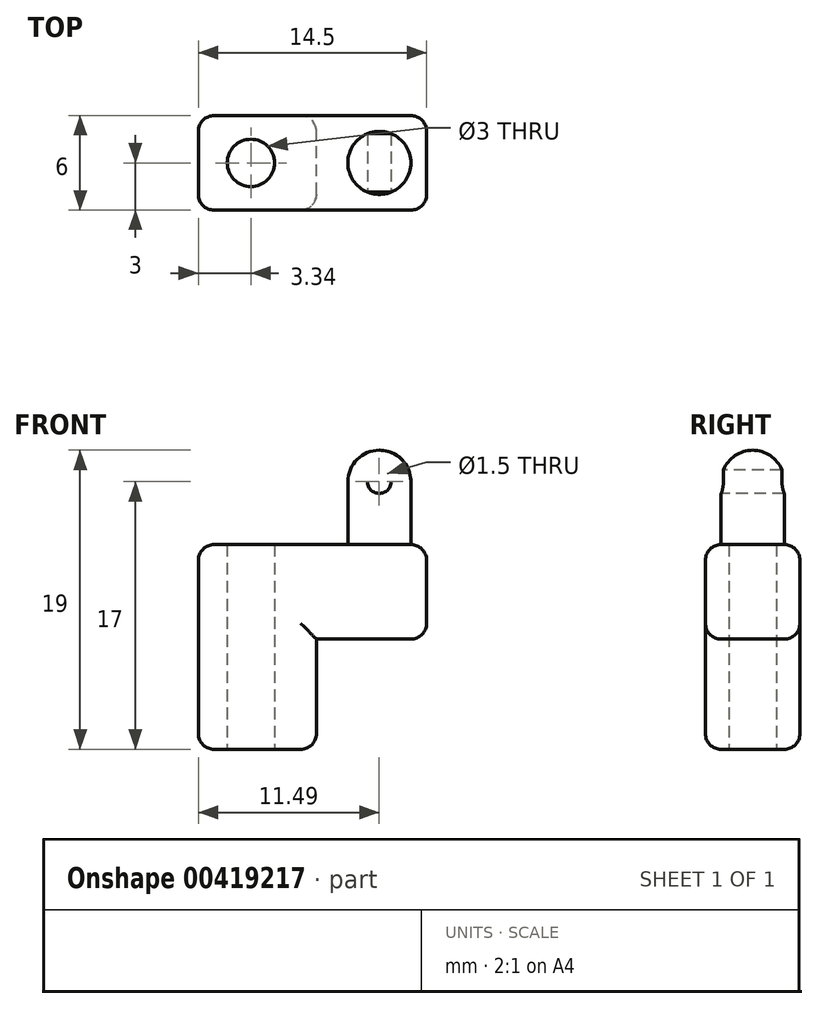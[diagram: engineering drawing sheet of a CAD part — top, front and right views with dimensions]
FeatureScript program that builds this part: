
annotation { "Feature Type Name" : "Feature", "Feature Type Description" : "" }
export const myFeature = defineFeature(function(context is Context, id is Id, definition is map)
    precondition{}
    {
        {
            var Q0;
            Q0=qCreatedBy(makeId("Front.planeOp"),FACE);
            var sketch = newSketch(context, id + "F0", { "sketchPlane" : qUnion([Q0])});
            skLineSegment(sketch, "E0", {"start": v(0, 0) * mm, "end": v(0, 13) * mm});
            skLineSegment(sketch, "E1", {"start": v(0, 13) * mm, "end": v(14.5, 13) * mm});
            skLineSegment(sketch, "E2", {"start": v(14.5, 13) * mm, "end": v(14.5, 7) * mm});
            skLineSegment(sketch, "E3", {"start": v(14.5, 7) * mm, "end": v(7.5, 7) * mm});
            skLineSegment(sketch, "E4", {"start": v(7.5, 7) * mm, "end": v(7.5, 0) * mm});
            skLineSegment(sketch, "E5", {"start": v(7.5, 0) * mm, "end": v(0, 0) * mm});
            skSolve(sketch);
        }
        {
            var Q0;
            Q0 = qSketchRegion(id + "F0", true);
            extrude(context, id + "F1", {"entities" : qUnion([Q0]), "endBound" : BoundingType.SYMMETRIC, "depth" : 6 * mm});
        }
        {
            var Q0;
            Q0=makeQuery(id+"F1.opExtrude","SWEPT_FACE",FACE,{"disambiguationData":[OSD([sQuery(id+"F0.wireOp",EDGE,"E1")])]});
            var sketch = newSketch(context, id + "F2", { "sketchPlane" : qUnion([Q0])});
            skCircle(sketch, "E6", {"center": v(11.5, 0) * mm, "radius": 2 * mm});
            skCircle(sketch, "E7", {"center": v(11.5, 0) * mm, "radius": 3 * mm, "construction": true});
            skSolve(sketch);
        }
        {
            var Q0;
            Q0=makeQuery(id+"F2.imprint","IMPRINT",FACE,{"disambiguationData":[TD([[makeQuery(id+"F2.imprint","IMPRINT",EDGE,{"derivedFrom":sQuery(id+"F2.wireOp",EDGE,"E6")}),1.0]])]});
            extrude(context, id + "F3", {"entities" : qUnion([Q0]), "operationType" : NewBodyOperationType.ADD, "depth" : 6 * mm});
        }
        {
            var Q0;
            Q0=makeQuery(id+"F3.opExtrude","CAP_EDGE",EDGE,{"disambiguationData":[OSD([sQuery(id+"F2.wireOp",EDGE,"E6")])],"isStart":false});
            fillet(context, id + "F4", {"entities" : qUnion([Q0]), "radius" : 2 * mm, "tangentPropagation" : true, "allowEdgeOverflow" : false});
        }
        {
            var Q0;
            Q0=qCreatedBy(makeId("Front.planeOp"),FACE);
            var sketch = newSketch(context, id + "F5", { "sketchPlane" : qUnion([Q0])});
            skCircle(sketch, "E8", {"center": v(11.5, 17) * mm, "radius": 0.75 * mm});
            skLineSegment(sketch, "E9.0", {"start": v(13.5, 17) * mm, "end": v(9.5, 17) * mm});
            skSolve(sketch);
        }
        {
            var Q0;
            Q0 = qSketchRegion(id + "F5", true);
            extrude(context, id + "F6", {"entities" : qUnion([Q0]), "operationType" : NewBodyOperationType.REMOVE, "endBound" : BoundingType.SYMMETRIC, "oppositeDirection" : true, "depth" : 25 * mm});
        }
        {
            var Q0;
            Q0=makeQuery(id+"F1.opExtrude","SWEPT_FACE",FACE,{"disambiguationData":[OSD([sQuery(id+"F0.wireOp",EDGE,"E5")])]});
            var sketch = newSketch(context, id + "F7", { "sketchPlane" : qUnion([Q0])});
            skPoint(sketch, "E10", {"position": v(3.34, 0) * mm});
            skPoint(sketch, "E11", {"position": v(3.34, 3) * mm});
            skSolve(sketch);
        }
        {
            var Q0;
            Q0=sQuery(id+"F7.wireOp",VERTEX,"E10");
            var Q1;
            Q1=makeQuery(id+"F1.opExtrude","SWEPT_BODY",BODY,{"disambiguationData":[OSD([sQuery(id+"F0.wireOp",EDGE,"E0"),sQuery(id+"F0.wireOp",EDGE,"E1"),sQuery(id+"F0.wireOp",EDGE,"E2"),sQuery(id+"F0.wireOp",EDGE,"E3"),sQuery(id+"F0.wireOp",EDGE,"E4"),sQuery(id+"F0.wireOp",EDGE,"E5")])]});
            hole(context, id + "F8", {"style" : HoleStyle.SIMPLE, "endStyle" : HoleEndStyle.THROUGH, "holeDiameter" : 3 * mm, "isTappedThrough" : true, "tappedDepth" : 12 * mm, "tapClearance" : 3, "locations" : qUnion([Q0]), "scope" : qUnion([Q1])});
        }
        {
            var Q0;
            Q0=makeQuery(id+"F1.opExtrude","CAP_EDGE",EDGE,{"disambiguationData":[OSD([sQuery(id+"F0.wireOp",EDGE,"E0")])],"isStart":true});
            var Q1;
            Q1=makeQuery(id+"F1.opExtrude","CAP_EDGE",EDGE,{"disambiguationData":[OSD([sQuery(id+"F0.wireOp",EDGE,"E1")])],"isStart":true});
            var Q2;
            Q2=makeQuery(id+"F1.opExtrude","CAP_EDGE",EDGE,{"disambiguationData":[OSD([sQuery(id+"F0.wireOp",EDGE,"E2")])],"isStart":true});
            var Q3;
            Q3=makeQuery(id+"F1.opExtrude","CAP_EDGE",EDGE,{"disambiguationData":[OSD([sQuery(id+"F0.wireOp",EDGE,"E3")])],"isStart":true});
            var Q4;
            Q4=makeQuery(id+"F1.opExtrude","CAP_FACE",FACE,{"disambiguationData":[OSD([sQuery(id+"F0.wireOp",EDGE,"E0"),sQuery(id+"F0.wireOp",EDGE,"E1"),sQuery(id+"F0.wireOp",EDGE,"E2"),sQuery(id+"F0.wireOp",EDGE,"E3"),sQuery(id+"F0.wireOp",EDGE,"E4"),sQuery(id+"F0.wireOp",EDGE,"E5")])],"isStart":true});
            var Q5;
            Q5=makeQuery(id+"F1.opExtrude","CAP_EDGE",EDGE,{"disambiguationData":[OSD([sQuery(id+"F0.wireOp",EDGE,"E5")])],"isStart":true});
            var Q6;
            Q6=makeQuery(id+"F1.opExtrude","CAP_EDGE",EDGE,{"disambiguationData":[OSD([sQuery(id+"F0.wireOp",EDGE,"E4")])],"isStart":true});
            var Q7;
            Q7=makeQuery(id+"F1.opExtrude","CAP_EDGE",EDGE,{"disambiguationData":[OSD([sQuery(id+"F0.wireOp",EDGE,"E0")])],"isStart":false});
            var Q8;
            Q8=makeQuery(id+"F1.opExtrude","CAP_EDGE",EDGE,{"disambiguationData":[OSD([sQuery(id+"F0.wireOp",EDGE,"E4")])],"isStart":false});
            var Q9;
            Q9=makeQuery(id+"F1.opExtrude","CAP_EDGE",EDGE,{"disambiguationData":[OSD([sQuery(id+"F0.wireOp",EDGE,"E5")])],"isStart":false});
            var Q10;
            Q10=makeQuery(id+"F1.opExtrude","CAP_EDGE",EDGE,{"disambiguationData":[OSD([sQuery(id+"F0.wireOp",EDGE,"E1")])],"isStart":false});
            var Q11;
            Q11=makeQuery(id+"F1.opExtrude","CAP_EDGE",EDGE,{"disambiguationData":[OSD([sQuery(id+"F0.wireOp",EDGE,"E2")])],"isStart":false});
            var Q12;
            Q12=makeQuery(id+"F1.opExtrude","SWEPT_EDGE",EDGE,{"disambiguationData":[OSD([sQuery(id+"F0.wireOp",EDGE,"E0"),sQuery(id+"F0.wireOp",EDGE,"E1")])]});
            var Q13;
            Q13=makeQuery(id+"F1.opExtrude","SWEPT_EDGE",EDGE,{"disambiguationData":[OSD([sQuery(id+"F0.wireOp",EDGE,"E0"),sQuery(id+"F0.wireOp",EDGE,"E5")])]});
            var Q14;
            Q14=makeQuery(id+"F1.opExtrude","SWEPT_EDGE",EDGE,{"disambiguationData":[OSD([sQuery(id+"F0.wireOp",EDGE,"E4"),sQuery(id+"F0.wireOp",EDGE,"E5")])]});
            var Q15;
            Q15=makeQuery(id+"F1.opExtrude","CAP_EDGE",EDGE,{"disambiguationData":[OSD([sQuery(id+"F0.wireOp",EDGE,"E3")])],"isStart":false});
            var Q16;
            Q16=makeQuery(id+"F1.opExtrude","SWEPT_EDGE",EDGE,{"disambiguationData":[OSD([sQuery(id+"F0.wireOp",EDGE,"E1"),sQuery(id+"F0.wireOp",EDGE,"E2")])]});
            var Q17;
            Q17=makeQuery(id+"F1.opExtrude","SWEPT_EDGE",EDGE,{"disambiguationData":[OSD([sQuery(id+"F0.wireOp",EDGE,"E2"),sQuery(id+"F0.wireOp",EDGE,"E3")])]});
            fillet(context, id + "F9", {"entities" : qUnion([Q0, Q1, Q2, Q3, Q4, Q5, Q6, Q7, Q8, Q9, Q10, Q11, Q12, Q13, Q14, Q15, Q16, Q17]), "radius" : 1 * mm, "tangentPropagation" : true, "allowEdgeOverflow" : false});
        }
    });
